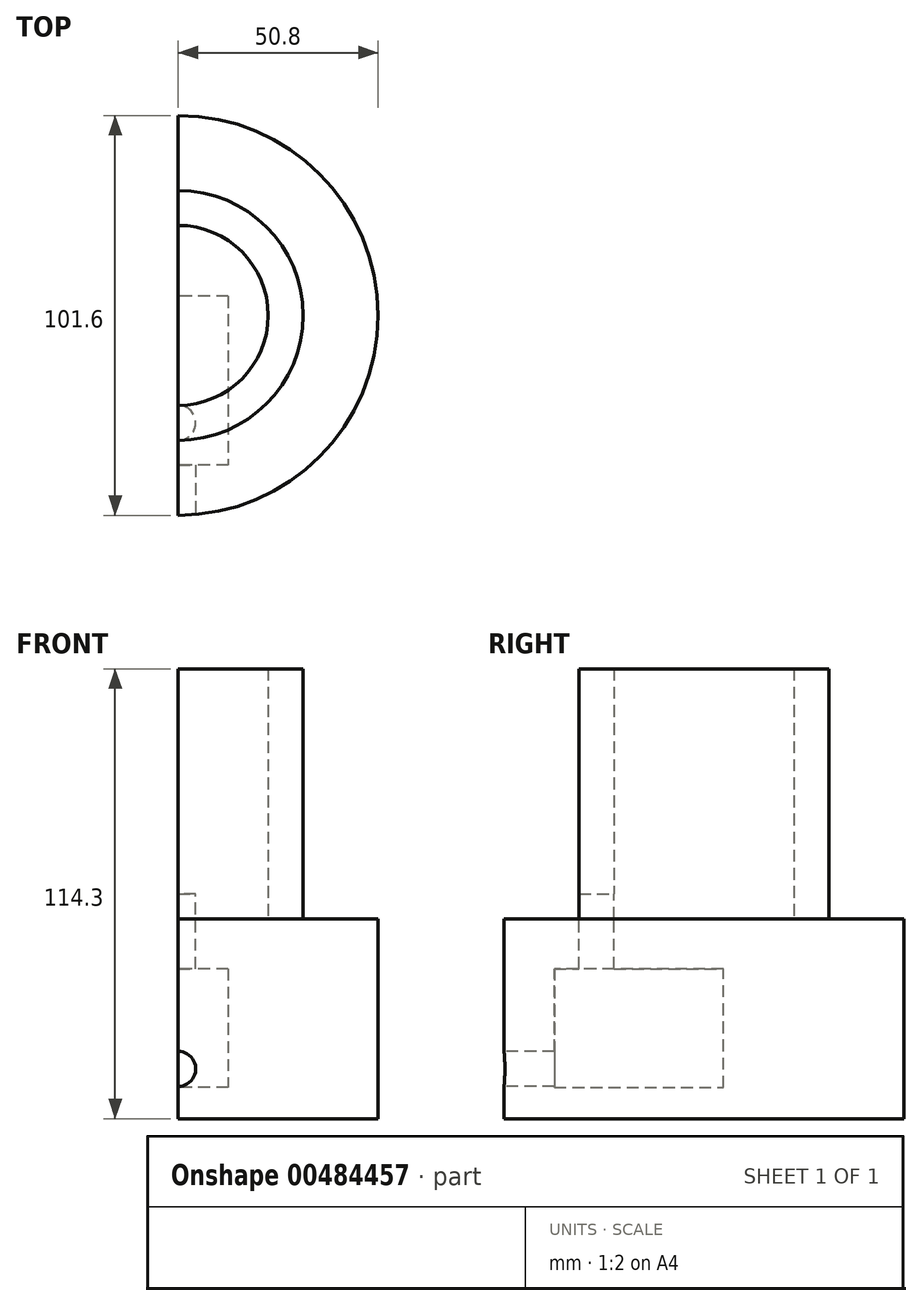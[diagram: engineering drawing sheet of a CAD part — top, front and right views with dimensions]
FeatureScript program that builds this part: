
annotation { "Feature Type Name" : "Feature", "Feature Type Description" : "" }
export const myFeature = defineFeature(function(context is Context, id is Id, definition is map)
    precondition{}
    {
        {
            var Q0;
            Q0=qCreatedBy(makeId("Top.planeOp"),FACE);
            cPlane(context, id + "F0", {"entities" : qUnion([Q0]), "cplaneType" : CPlaneType.OFFSET, "offset" : 12.7 * mm, "width" : 152.4 * mm, "height" : 152.4 * mm});
        }
        {
            var Q0;
            Q0=qCreatedBy(id+"F0.planeOp",FACE);
            var sketch = newSketch(context, id + "F1", { "sketchPlane" : qUnion([Q0])});
            skCircle(sketch, "E0", {"center": v(0, 0) * mm, "radius": 50.8 * mm});
            skSolve(sketch);
        }
        {
            var Q0;
            Q0=makeQuery(id+"F1.imprint","IMPRINT",FACE,{"disambiguationData":[TD([[makeQuery(id+"F1.imprint","IMPRINT",EDGE,{"derivedFrom":sQuery(id+"F1.wireOp",EDGE,"E0")}),1.0]])]});
            extrude(context, id + "F2", {"entities" : qUnion([Q0]), "oppositeDirection" : true, "depth" : 50.8 * mm});
        }
        {
            var Q0;
            Q0=qCreatedBy(makeId("Front.planeOp"),FACE);
            cPlane(context, id + "F3", {"entities" : qUnion([Q0]), "cplaneType" : CPlaneType.OFFSET, "offset" : 50.8 * mm, "width" : 152.4 * mm, "height" : 152.4 * mm});
        }
        {
            var Q0;
            Q0=qCreatedBy(id+"F3.planeOp",FACE);
            var sketch = newSketch(context, id + "F4", { "sketchPlane" : qUnion([Q0])});
            skCircle(sketch, "E1", {"center": v(0, -25.46) * mm, "radius": 4.45 * mm});
            skSolve(sketch);
        }
        {
            var Q0;
            Q0=makeQuery(id+"F4.imprint","IMPRINT",FACE,{"disambiguationData":[TD([[makeQuery(id+"F4.imprint","IMPRINT",EDGE,{"derivedFrom":sQuery(id+"F4.wireOp",EDGE,"E1")}),1.0]])]});
            extrude(context, id + "F5", {"entities" : qUnion([Q0]), "operationType" : NewBodyOperationType.REMOVE, "oppositeDirection" : true, "depth" : 15.24 * mm});
        }
        {
            var Q0;
            Q0=makeQuery(id+"F4.imprint","IMPRINT",FACE,{"disambiguationData":[TD([[makeQuery(id+"F4.imprint","IMPRINT",EDGE,{"derivedFrom":sQuery(id+"F4.wireOp",EDGE,"E1")}),1.0]])]});
            extrude(context, id + "F6", {"entities" : qUnion([Q0]), "operationType" : NewBodyOperationType.REMOVE, "oppositeDirection" : true, "depth" : 12.7 * mm});
        }
        {
            var Q0;
            Q0=qCreatedBy(makeId("Right.planeOp"),FACE);
            var sketch = newSketch(context, id + "F7", { "sketchPlane" : qUnion([Q0])});
            skLineSegment(sketch, "E2", {"start": v(4.88, 0) * mm, "end": v(-4.34, 0) * mm});
            skLineSegment(sketch, "E3.bottom", {"start": v(4.88, 0) * mm, "end": v(-38.03, 0) * mm});
            skLineSegment(sketch, "E3.top", {"start": v(4.88, -30.2) * mm, "end": v(-38.03, -30.2) * mm});
            skLineSegment(sketch, "E3.left", {"start": v(4.88, 0) * mm, "end": v(4.88, -30.2) * mm});
            skLineSegment(sketch, "E3.right", {"start": v(-38.03, 0) * mm, "end": v(-38.03, -30.2) * mm});
            skSolve(sketch);
        }
        {
            var Q0;
            Q0=makeQuery(id+"F7.imprint","IMPRINT",FACE,{"disambiguationData":[TD([[makeQuery(id+"F7.imprint","IMPRINT",EDGE,{"derivedFrom":sQuery(id+"F7.wireOp",EDGE,"E3.top")}),-1.0]])]});
            extrude(context, id + "F8", {"entities" : qUnion([Q0]), "operationType" : NewBodyOperationType.REMOVE, "depth" : 12.7 * mm});
        }
        {
            var Q0;
            Q0=makeQuery(id+"F7.imprint","IMPRINT",FACE,{"disambiguationData":[TD([[makeQuery(id+"F7.imprint","IMPRINT",EDGE,{"derivedFrom":sQuery(id+"F7.wireOp",EDGE,"E3.top")}),-1.0]])]});
            extrude(context, id + "F9", {"entities" : qUnion([Q0]), "operationType" : NewBodyOperationType.REMOVE, "oppositeDirection" : true, "depth" : 25.4 * mm});
        }
        {
            var Q0;
            Q0=qCreatedBy(id+"F0.planeOp",FACE);
            var sketch = newSketch(context, id + "F10", { "sketchPlane" : qUnion([Q0])});
            skCircle(sketch, "E4", {"center": v(0, 0) * mm, "radius": 31.75 * mm});
            skCircle(sketch, "E5.0", {"center": v(0, 0) * mm, "radius": 22.86 * mm});
            skSolve(sketch);
        }
        {
            var Q0;
            Q0=makeQuery(id+"F10.imprint","IMPRINT",FACE,{"disambiguationData":[TD([[makeQuery(id+"F10.imprint","IMPRINT",EDGE,{"derivedFrom":sQuery(id+"F10.wireOp",EDGE,"E4")}),1.0]])]});
            extrude(context, id + "F11", {"entities" : qUnion([Q0]), "operationType" : NewBodyOperationType.ADD, "depth" : 63.5 * mm});
        }
        {
            var Q0;
            Q0=makeQuery(id+"F11.opExtrude","CAP_FACE",FACE,{"disambiguationData":[OSD([sQuery(id+"F10.wireOp",EDGE,"E4"),sQuery(id+"F10.wireOp",EDGE,"E5.0")])],"isStart":false});
            cPlane(context, id + "F12", {"entities" : qUnion([Q0]), "cplaneType" : CPlaneType.OFFSET, "offset" : 0 * mm, "width" : 152.4 * mm, "height" : 152.4 * mm});
        }
        {
            var Q0;
            Q0=qCreatedBy(id+"F12.planeOp",FACE);
            var sketch = newSketch(context, id + "F13", { "sketchPlane" : qUnion([Q0])});
            skLineSegment(sketch, "E6.bottom", {"start": v(0, 55.95) * mm, "end": v(-63.24, 55.95) * mm});
            skLineSegment(sketch, "E6.top", {"start": v(0, -67.24) * mm, "end": v(-63.24, -67.24) * mm});
            skLineSegment(sketch, "E6.left", {"start": v(0, 55.95) * mm, "end": v(0, -67.24) * mm});
            skLineSegment(sketch, "E6.right", {"start": v(-63.24, 55.95) * mm, "end": v(-63.24, -67.24) * mm});
            skSolve(sketch);
        }
        {
            var Q0;
            Q0=makeQuery(id+"F13.imprint","IMPRINT",FACE,{"disambiguationData":[TD([[makeQuery(id+"F13.imprint","IMPRINT",EDGE,{"derivedFrom":sQuery(id+"F13.wireOp",EDGE,"E6.bottom")}),1.0]])]});
            extrude(context, id + "F14", {"entities" : qUnion([Q0]), "operationType" : NewBodyOperationType.REMOVE, "oppositeDirection" : true, "depth" : 127 * mm});
        }
        {
            var Q0;
            Q0=qCreatedBy(id+"F0.planeOp",FACE);
            cPlane(context, id + "F15", {"entities" : qUnion([Q0]), "cplaneType" : CPlaneType.OFFSET, "offset" : 6.35 * mm, "width" : 152.4 * mm, "height" : 152.4 * mm});
        }
        {
            var Q0;
            Q0=qCreatedBy(id+"F15.planeOp",FACE);
            var sketch = newSketch(context, id + "F16", { "sketchPlane" : qUnion([Q0])});
            skCircle(sketch, "E7", {"center": v(0, -27.3) * mm, "radius": 4.45 * mm});
            skSolve(sketch);
        }
        {
            var Q0;
            Q0=makeQuery(id+"F16.imprint","IMPRINT",FACE,{"disambiguationData":[TD([[makeQuery(id+"F16.imprint","IMPRINT",EDGE,{"derivedFrom":sQuery(id+"F16.wireOp",EDGE,"E7")}),1.0]])]});
            extrude(context, id + "F17", {"entities" : qUnion([Q0]), "operationType" : NewBodyOperationType.REMOVE, "oppositeDirection" : true, "depth" : 25.4 * mm});
        }
        {
            var Q0;
            Q0=qCreatedBy(makeId("Right.planeOp"),FACE);
            cPlane(context, id + "F18", {"entities" : qUnion([Q0]), "cplaneType" : CPlaneType.OFFSET, "offset" : 31.75 * mm, "width" : 152.4 * mm, "height" : 152.4 * mm});
        }
    });
